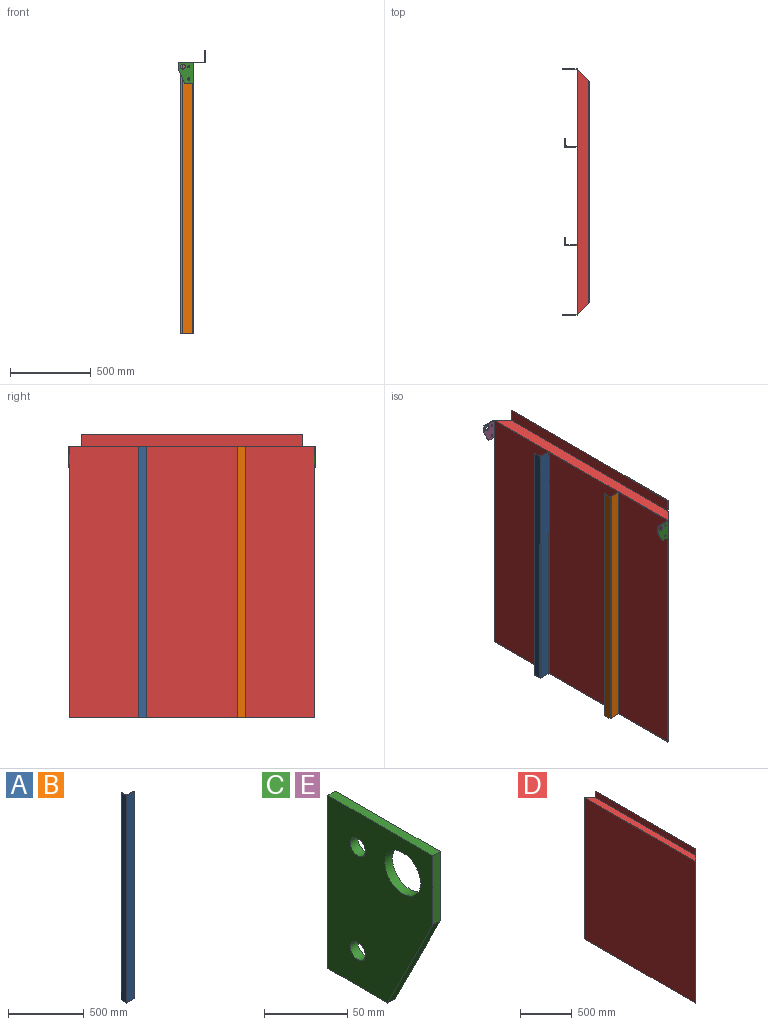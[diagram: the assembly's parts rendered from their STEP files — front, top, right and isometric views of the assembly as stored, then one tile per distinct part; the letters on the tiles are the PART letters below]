
ASSEMBLY  parts=5 mates=3
PART A: 11 faces, bbox 76.2x50.8x1676.4 mm
  f0: plane 76.2x50.8mm, normal (0,0,-1), area 591.4mm2, adj f2,f3,f4,f5,f6,f7,f8,f9
  f1: plane 76.2x50.8mm, normal (0,0,1), area 591.4mm2, adj f2,f3,f4,f5,f6,f7,f8,f9
  f2: plane 1676.4x60.33mm, normal (0,1,0), area 101128.9mm2, adj f0,f1,f3,f10
  f3: cylinder r=7.94mm len=1676.4mm, axis (0,0,1), area 20901.9mm2, adj f0,f1,f2,f4
  f4: plane 1676.4x34.93mm, normal (1,0,0), area 58548.4mm2, adj f0,f1,f3,f5
  f5: cylinder r=3.17mm len=1676.4mm, axis (0,0,-1), area 8360.3mm2, adj f0,f1,f4,f6
  f6: plane 1676.4x1.59mm, normal (0,1,0), area 2661.5mm2, adj f0,f1,f5,f7
  f7: plane 1676.4x50.8mm, normal (-1,0,0), area 85161.1mm2, adj f0,f1,f6,f8
  f8: plane 1676.4x76.2mm, normal (0,-1,0), area 127741.7mm2, adj f0,f1,f7,f9
  f9: plane 1676.4x1.59mm, normal (1,0,0), area 2661.5mm2, adj f0,f1,f8,f10
  f10: cylinder r=3.17mm len=1676.4mm, axis (0,0,1), area 8360.3mm2, adj f0,f1,f2,f9
PART B: same geometry as A
PART C: 10 faces, bbox 6.4x88.9x127 mm
  f0: plane 127x6.35mm, normal (0,1,0), area 806.5mm2, adj f1,f7,f8,f9
  f1: plane 50.8x6.35mm, normal (0,0,-1), area 322.6mm2, adj f0,f2,f8,f9
  f2: plane 76.2x38.1mm, normal (0,-0.89,-0.45), area 541mm2, adj f1,f3,f8,f9
  f3: plane 50.8x6.35mm, normal (0,-1,0), area 322.6mm2, adj f2,f7,f8,f9
  f4: cylinder r=6.35mm len=12.7mm, axis (-1,0,0), area 253.4mm2, adj f8,f9
  f5: cylinder r=6.35mm len=12.7mm, axis (-1,0,0), area 253.4mm2, adj f8,f9
  f6: cylinder r=15.08mm len=30.16mm, axis (-1,0,0), area 601.7mm2, adj f8,f9
  f7: plane 88.9x6.35mm, normal (0,0,1), area 564.5mm2, adj f0,f3,f8,f9
  f8: plane 127x88.9mm, normal (1,0,0), area 8870.8mm2, adj f0,f1,f2,f3,f4,f5,f6,f7
  f9: plane 127x88.9mm, normal (-1,0,0), area 8870.8mm2, adj f0,f1,f2,f3,f4,f5,f6,f7
PART D: 16 faces, bbox 76.2x1518.7x1752.6 mm
  f0: plane 1676.4x1518.69mm, normal (-1,0,0), area 2545925.7mm2, adj f2,f4,f10,f13
  f1: plane 1371.6x76.2mm, normal (-1,0,0), area 104515.9mm2, adj f2,f5,f12,f15
  f2: plane 1518.69x73.54mm, normal (0,0,1), area 106664.1mm2, adj f0,f1,f6,f7,f10,f11,f13,f14
  f3: plane 1518.69x73.54mm, normal (0,0,-1), area 106273.3mm2, adj f6,f7,f8,f9,f11,f12,f14,f15
  f4: plane 1518.69x2.66mm, normal (0,0,-1), area 4034.9mm2, adj f0,f9,f10,f13
  f5: plane 1371.6x2.66mm, normal (0,0,1), area 3644.1mm2, adj f1,f8,f12,f15
  f6: plane 70.89x70.89mm, normal (0.71,-0.71,0), area 266.3mm2, adj f2,f3,f10,f11
  f7: plane 70.89x70.89mm, normal (0.71,0.71,0), area 266.3mm2, adj f2,f3,f13,f14
  f8: plane 1371.6x78.86mm, normal (1,0,0), area 108160mm2, adj f3,f5,f12,f15
  f9: plane 1673.74x1518.69mm, normal (1,0,0), area 2541890.8mm2, adj f3,f4,f10,f13
  f10: plane 1676.4x2.66mm, normal (0,-1,0), area 4453.9mm2, adj f0,f2,f4,f6,f9
  f11: plane 2.66x2.66mm, normal (1,0,0), area 7.1mm2, adj f2,f3,f6,f12
  f12: plane 78.86x2.66mm, normal (0,-1,0), area 209.5mm2, adj f1,f3,f5,f8,f11
  f13: plane 1676.4x2.66mm, normal (0,1,0), area 4453.9mm2, adj f0,f2,f4,f7,f9
  f14: plane 2.66x2.66mm, normal (1,0,0), area 7.1mm2, adj f2,f3,f7,f15
  f15: plane 78.86x2.66mm, normal (0,1,0), area 209.5mm2, adj f1,f3,f5,f8,f14
PART E: same geometry as C
PLACE A t=(1184.7,2060.56,-725.3)mm
PLACE B t=(1184.7,1450.96,-725.3)mm
PLACE C rot(axis=(0,0,-1),90deg) t=(879.9,-41.29,-725.3)mm
PLACE D t=(1184.7,1781.16,-725.3)mm
PLACE E rot(axis=(0,0,-1),90deg) t=(879.9,1476.36,-725.3)mm
MATE fastened E.f7 <-> D.f2  axis (0,0,1) through (117.9,2543.16,3237.1)mm
MATE fastened C.f7 <-> D.f2  axis (0,0,1) through (117.9,1019.16,3237.1)mm
MATE fastened B.f0 <-> D.f4  axis (0,0,-1) through (117.9,1450.96,1560.7)mm
